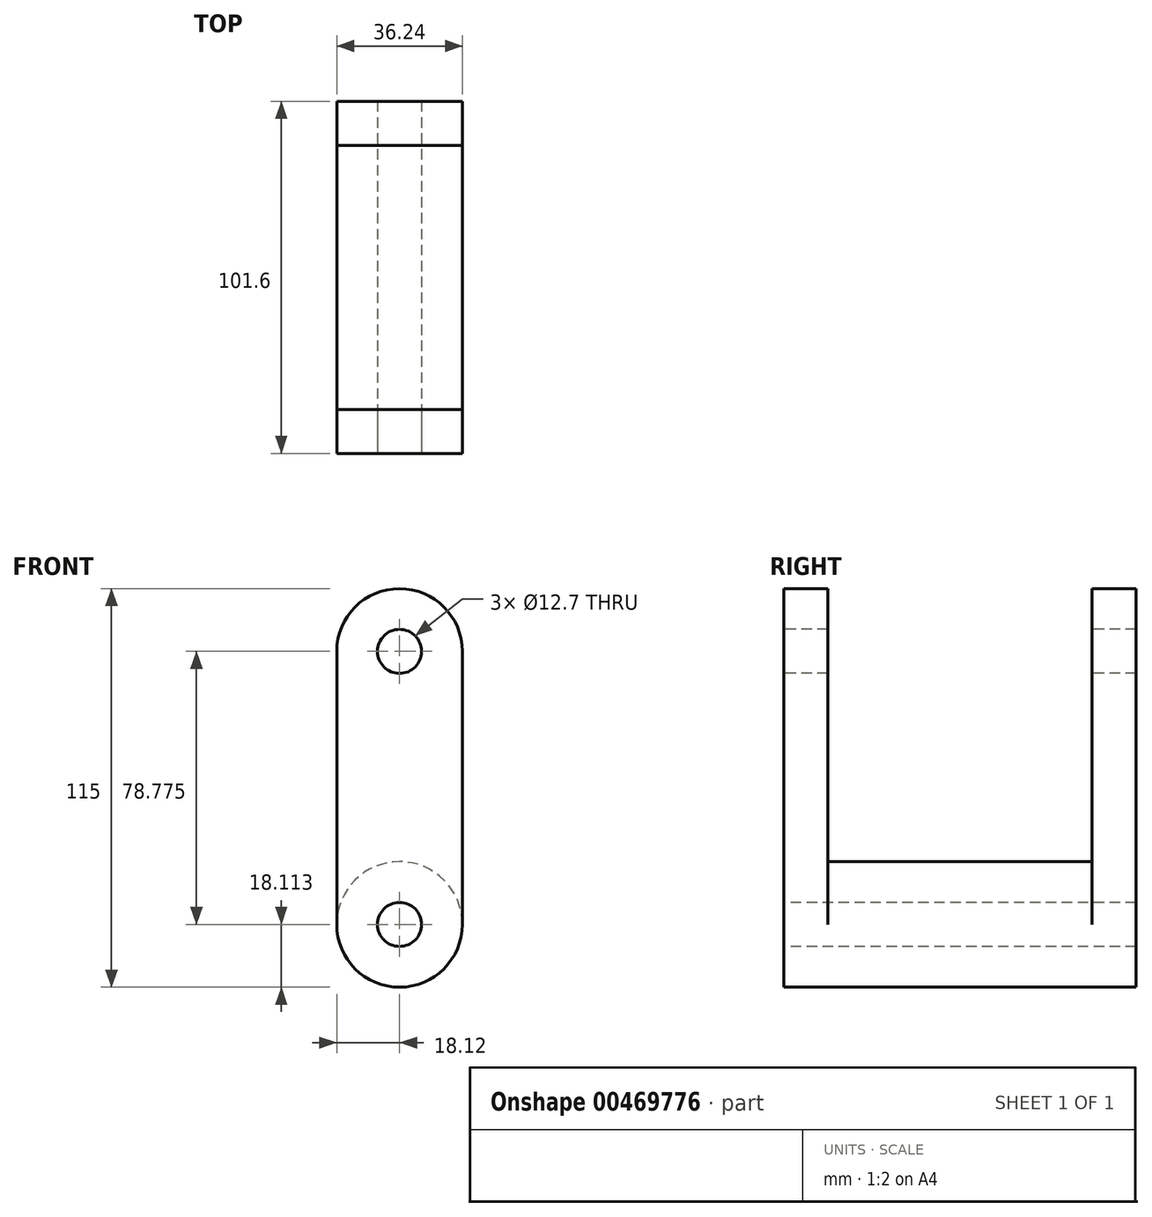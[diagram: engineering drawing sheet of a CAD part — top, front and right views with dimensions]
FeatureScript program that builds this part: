
annotation { "Feature Type Name" : "Feature", "Feature Type Description" : "" }
export const myFeature = defineFeature(function(context is Context, id is Id, definition is map)
    precondition{}
    {
        {
            var Q0;
            Q0=qCreatedBy(makeId("Front.planeOp"),FACE);
            var sketch = newSketch(context, id + "F0", { "sketchPlane" : qUnion([Q0])});
            skLineSegment(sketch, "E0.left", {"start": v(-18.12, 39.39) * mm, "end": v(-18.12, -39.39) * mm});
            skLineSegment(sketch, "E0.right", {"start": v(18.12, 39.39) * mm, "end": v(18.12, -39.39) * mm});
            skPoint(sketch, "E0.middle", {"position": v(0, 0) * mm});
            skCircle(sketch, "E1", {"center": v(0, -39.39) * mm, "radius": 18.12 * mm});
            skArc(sketch, "E2", {"start": v(18.12, 39.39) * mm, "mid": v(0, 57.5) * mm, "end": v(-18.12, 39.39) * mm});
            skSolve(sketch);
        }
        {
            var Q0;
            {var subQ0=sQuery(id+"F0.wireOp",EDGE,"E0.left");Q0=makeQuery(id+"F0.imprint","IMPRINT",FACE,{"disambiguationData":[TD([[makeQuery(id+"F0.imprint","IMPRINT",EDGE,{"derivedFrom":subQ0}),1.0]])]});}
            extrude(context, id + "F1", {"entities" : qUnion([Q0]), "oppositeDirection" : true, "depth" : 12.7 * mm});
        }
        {
            var Q0;
            Q0=makeQuery(id+"F1.opExtrude","CAP_FACE",FACE,{"disambiguationData":[OSD([sQuery(id+"F0.wireOp",EDGE,"E0.left"),sQuery(id+"F0.wireOp",EDGE,"E0.right"),sQuery(id+"F0.wireOp",EDGE,"E1"),sQuery(id+"F0.wireOp",EDGE,"E2")])],"isStart":true});
            var sketch = newSketch(context, id + "F2", { "sketchPlane" : qUnion([Q0])});
            skCircle(sketch, "E3", {"center": v(0, -39.39) * mm, "radius": 18.12 * mm});
            skSolve(sketch);
        }
        {
            var Q0;
            {var subQ0=sQuery(id+"F2.wireOp",EDGE,"E3");var subQ1=makeQuery(id+"F2.imprint","INTERSECT",VERTEX,{"derivedFrom":[makeQuery(id+"F1.opExtrude","CAP_EDGE",EDGE,{"disambiguationData":[OSD([sQuery(id+"F0.wireOp",EDGE,"E0.left")])],"isStart":true}),subQ0]});Q0=makeQuery(id+"F2.imprint","IMPRINT",FACE,{"disambiguationData":[TD([[makeQuery(id+"F2.imprint","IMPRINT",EDGE,{"disambiguationData":[TD([[subQ1,1.0]])],"derivedFrom":subQ0}),1.0]])]});}
            extrude(context, id + "F3", {"entities" : qUnion([Q0]), "operationType" : NewBodyOperationType.ADD, "oppositeDirection" : true, "depth" : 50.8 * mm});
        }
        {
            var Q0;
            Q0=qCreatedBy(makeId("Front.planeOp"),FACE);
            cPlane(context, id + "F4", {"entities" : qUnion([Q0]), "cplaneType" : CPlaneType.OFFSET, "offset" : 50.8 * mm, "oppositeDirection" : true, "width" : 152.4 * mm, "height" : 152.4 * mm});
        }
        {
            var Q0;
            Q0=makeQuery(id+"F1.opExtrude","SWEPT_BODY",BODY,{"disambiguationData":[OSD([sQuery(id+"F0.wireOp",EDGE,"E0.left"),sQuery(id+"F0.wireOp",EDGE,"E0.right"),sQuery(id+"F0.wireOp",EDGE,"E1"),sQuery(id+"F0.wireOp",EDGE,"E2")])]});
            var Q1;
            Q1=qCreatedBy(id+"F4.planeOp",FACE);
            mirror(context, id + "F5", {"operationType" : NewBodyOperationType.ADD, "entities" : qUnion([Q0]), "mirrorPlane" : qUnion([Q1])});
        }
        {
            var Q0;
            Q0=makeQuery(id+"F3.boolean.opBoolean","MERGE",FACE,{"derivedFrom":[makeQuery(id+"F1.opExtrude","CAP_FACE",FACE,{"disambiguationData":[OSD([sQuery(id+"F0.wireOp",EDGE,"E0.left"),sQuery(id+"F0.wireOp",EDGE,"E0.right"),sQuery(id+"F0.wireOp",EDGE,"E1"),sQuery(id+"F0.wireOp",EDGE,"E2")])],"isStart":true}),makeQuery(id+"F3.opExtrude","CAP_FACE",FACE,{"disambiguationData":[OSD([sQuery(id+"F2.wireOp",EDGE,"E3")])],"isStart":true})]});
            var sketch = newSketch(context, id + "F6", { "sketchPlane" : qUnion([Q0])});
            skPoint(sketch, "E4", {"position": v(0, -39.39) * mm});
            skPoint(sketch, "E5", {"position": v(0, 39.39) * mm});
            skSolve(sketch);
        }
        {
            var Q0;
            Q0=sQuery(id+"F6.wireOp",VERTEX,"E4");
            var Q1;
            Q1=sQuery(id+"F6.wireOp",VERTEX,"E5");
            var Q2;
            Q2=makeQuery(id+"F1.opExtrude","SWEPT_BODY",BODY,{"disambiguationData":[OSD([sQuery(id+"F0.wireOp",EDGE,"E0.left"),sQuery(id+"F0.wireOp",EDGE,"E0.right"),sQuery(id+"F0.wireOp",EDGE,"E1"),sQuery(id+"F0.wireOp",EDGE,"E2")])]});
            hole(context, id + "F7", {"style" : HoleStyle.SIMPLE, "endStyle" : HoleEndStyle.THROUGH, "holeDiameter" : 12.7 * mm, "isTappedThrough" : true, "tappedDepth" : 12.7 * mm, "tapClearance" : 3, "locations" : qUnion([Q0, Q1]), "scope" : qUnion([Q2])});
        }
    });
